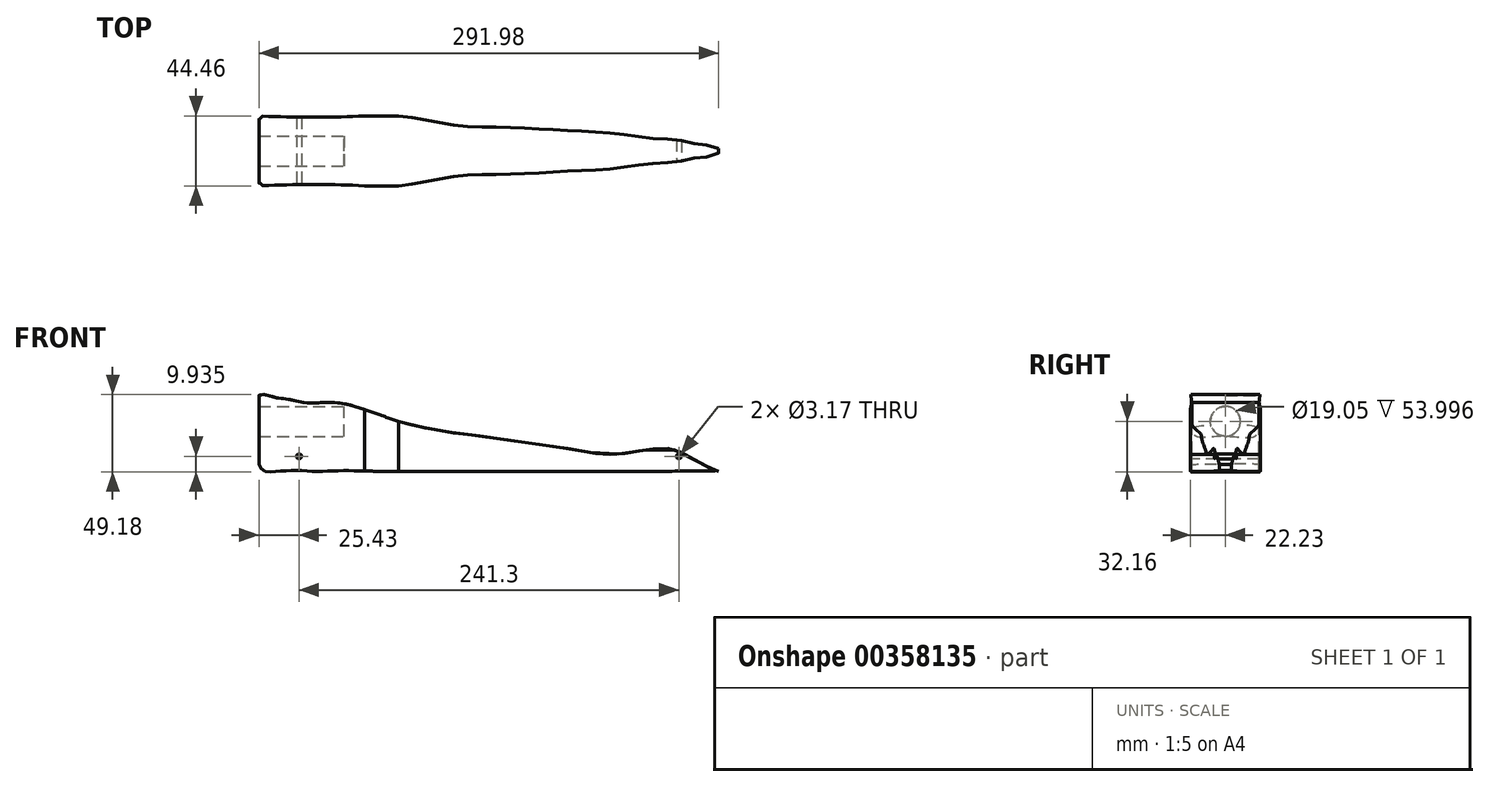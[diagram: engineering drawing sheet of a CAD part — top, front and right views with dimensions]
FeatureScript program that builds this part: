
annotation { "Feature Type Name" : "Feature", "Feature Type Description" : "" }
export const myFeature = defineFeature(function(context is Context, id is Id, definition is map)
    precondition{}
    {
        {
            var Q0;
            Q0=qCreatedBy(makeId("Front.planeOp"),FACE);
            var sketch = newSketch(context, id + "F0", { "sketchPlane" : qUnion([Q0])});
            skLineSegment(sketch, "E0.bottom", {"start": v(-146.05, 31.75) * mm, "end": v(146.05, 31.75) * mm, "construction": true});
            skLineSegment(sketch, "E0.top", {"start": v(-146.05, -31.75) * mm, "end": v(145.89, -31.75) * mm, "construction": true});
            skLineSegment(sketch, "E0.right", {"start": v(146.05, 31.75) * mm, "end": v(146.05, -31.75) * mm, "construction": true});
            skFitSpline(sketch, "E1", {"points": [v(-144.77, -30.17) * mm, v(-146.05, -3.37) * mm, v(-146.05, 16.5) * mm, v(-135.52, 15.06) * mm, v(-130.49, 14.37) * mm, v(-126.38, 13.8) * mm, v(-114.89, 11.7) * mm, v(-94.34, 11.55) * mm, v(-57.32, 0) * mm, v(-20.32, -7.57) * mm, v(0, -10.17) * mm, v(44.93, -16.57) * mm, v(67.35, -20.23) * mm, v(80.17, -21) * mm, v(109.64, -17.11) * mm, v(122.39, -19.95) * mm, v(138.81, -28.85) * mm, v(145.89, -31.75) * mm, v(142.7, -31.57) * mm, v(114.8, -31.75) * mm, v(102.73, -31.75) * mm, v(86.19, -31.75) * mm, v(70.47, -31.75) * mm, v(50.3, -31.75) * mm, v(20.04, -31.75) * mm, v(-5.77, -31.75) * mm, v(-26.32, -31.75) * mm, v(-71.12, -31.75) * mm, v(-95.56, -31.39) * mm, v(-110.2, -31.83) * mm, v(-119.42, -31.23) * mm, v(-133.3, -31.75) * mm, v(-144.77, -30.17) * mm]});
            skLineSegment(sketch, "E2.bottom", {"start": v(-146.05, 16.5) * mm, "end": v(-95.25, 9.52) * mm, "construction": true});
            skLineSegment(sketch, "E2.top", {"start": v(-146.05, -9.52) * mm, "end": v(-95.25, -9.52) * mm, "construction": true});
            skLineSegment(sketch, "E2.right", {"start": v(-95.25, 9.52) * mm, "end": v(-95.25, -9.52) * mm, "construction": true});
            skLineSegment(sketch, "E3", {"start": v(-146.05, 31.75) * mm, "end": v(-146.05, -31.75) * mm, "construction": true});
            skSolve(sketch);
        }
        {
            var Q0;
            Q0=qCreatedBy(makeId("Top.planeOp"),FACE);
            var sketch = newSketch(context, id + "F1", { "sketchPlane" : qUnion([Q0])});
            skLineSegment(sketch, "E4.bottom", {"start": v(-146.05, 22.22) * mm, "end": v(146.05, 22.23) * mm, "construction": true});
            skLineSegment(sketch, "E4.top", {"start": v(-146.05, -22.23) * mm, "end": v(146.05, -22.22) * mm, "construction": true});
            skLineSegment(sketch, "E4.left", {"start": v(-146.05, 22.22) * mm, "end": v(-146.05, -22.23) * mm, "construction": true});
            skLineSegment(sketch, "E4.right", {"start": v(146.05, 22.22) * mm, "end": v(146.05, -22.22) * mm, "construction": true});
            skLineSegment(sketch, "E5", {"start": v(-146.05, 0) * mm, "end": v(146.05, 0) * mm, "construction": true});
            skFitSpline(sketch, "E6", {"points": [v(-146.05, 0) * mm, v(-146.02, 20.08) * mm, v(-145.62, 21.72) * mm, v(-141.82, 21.96) * mm, v(-93.94, 21.53) * mm, v(-57.4, 22.23) * mm, v(-20.81, 16.16) * mm, v(7.62, 14.97) * mm, v(57.84, 12.5) * mm, v(78.97, 11.14) * mm, v(104.22, 7.92) * mm, v(118.9, 7) * mm, v(128.56, 4.93) * mm, v(137.74, 3.8) * mm, v(146.05, 0) * mm], "startDerivative": vector(0, 335.54) * mm, "endDerivative": vector(0, -277.49) * mm});
            skFitSpline(sketch, "E7.MirrorCS", {"points": [v(-146.05, 0) * mm, v(-146.02, -20.08) * mm, v(-145.62, -21.72) * mm, v(-141.82, -21.96) * mm, v(-93.94, -21.53) * mm, v(-57.4, -22.23) * mm, v(-20.81, -16.16) * mm, v(7.62, -14.97) * mm, v(57.84, -12.5) * mm, v(78.97, -11.14) * mm, v(104.22, -7.92) * mm, v(118.9, -7) * mm, v(128.56, -4.93) * mm, v(137.74, -3.8) * mm, v(146.05, 0) * mm], "startDerivative": vector(0, -335.54) * mm, "endDerivative": vector(0, 277.49) * mm});
            skLineSegment(sketch, "E8.MirrorCS", {"start": v(-146.05, -22.23) * mm, "end": v(146.05, -22.23) * mm});
            skSolve(sketch);
        }
        {
            var Q0;
            Q0=qCreatedBy(makeId("Right.planeOp"),FACE);
            var sketch = newSketch(context, id + "F2", { "sketchPlane" : qUnion([Q0])});
            skCircle(sketch, "E9", {"center": v(0, 0) * mm, "radius": 9.53 * mm});
            skSolve(sketch);
        }
        {
            var Q0;
            Q0=qCreatedBy(makeId("Front.planeOp"),FACE);
            var sketch = newSketch(context, id + "F3", { "sketchPlane" : qUnion([Q0])});
            skCircle(sketch, "E10", {"center": v(-120.65, -22.22) * mm, "radius": 1.59 * mm});
            skCircle(sketch, "E11", {"center": v(120.65, -22.23) * mm, "radius": 1.59 * mm});
            skSolve(sketch);
        }
        {
            var Q0;
            Q0=qSketchRegion(id+"F0",true);
            extrude(context, id + "F4", {"entities" : qUnion([Q0]), "depth" : 44.45 * mm, "symmetric" : true});
        }
        {
            var Q0;
            Q0=qSketchRegion(id+"F1",true);
            extrude(context, id + "F5", {"entities" : qUnion([Q0]), "operationType" : NewBodyOperationType.INTERSECT, "endBound" : BoundingType.THROUGH_ALL, "oppositeDirection" : true, "depth" : 60.96 * mm, "hasSecondDirection" : true, "secondDirectionBound" : BoundingType.THROUGH_ALL, "secondDirectionOppositeDirection" : false, "secondDirectionDepth" : 25.4 * mm});
        }
        {
            var Q0;
            Q0=qSketchRegion(id+"F2",true);
            extrude(context, id + "F6", {"entities" : qUnion([Q0]), "operationType" : NewBodyOperationType.REMOVE, "oppositeDirection" : true, "depth" : 152.4 * mm, "hasSecondDirection" : true, "secondDirectionOppositeDirection" : true, "secondDirectionDepth" : 92.07 * mm});
        }
        {
            var Q0;
            Q0=qSketchRegion(id+"F3",true);
            extrude(context, id + "F7", {"entities" : qUnion([Q0]), "operationType" : NewBodyOperationType.REMOVE, "oppositeDirection" : true, "depth" : 50.8 * mm, "symmetric" : true});
        }
    });
